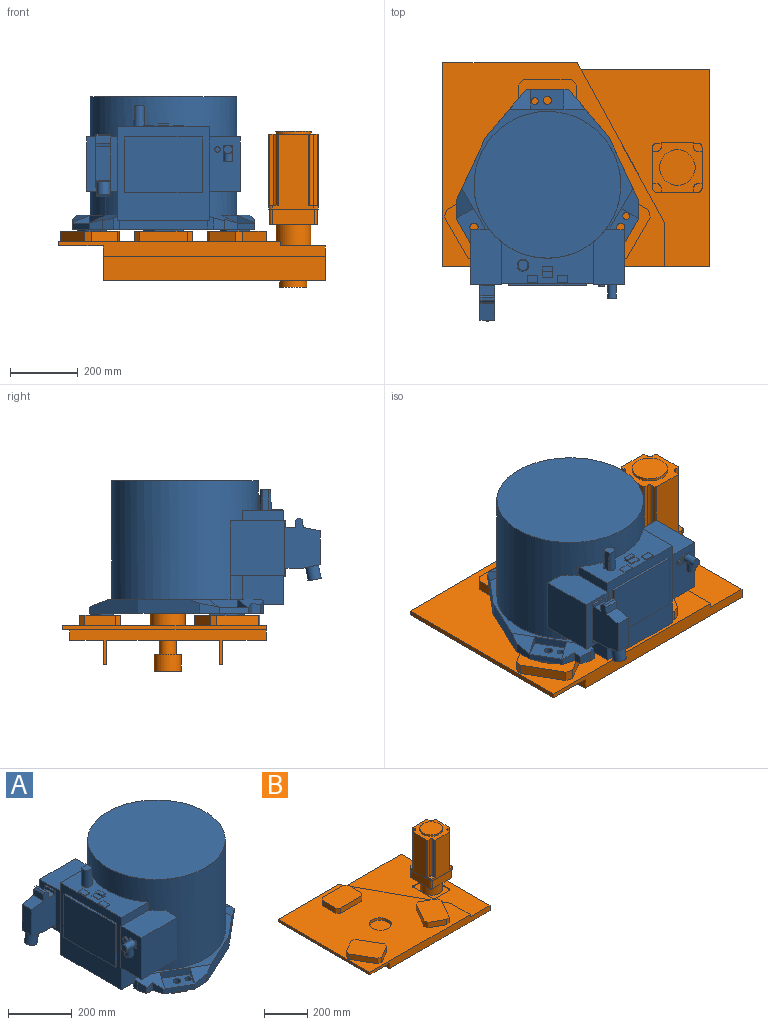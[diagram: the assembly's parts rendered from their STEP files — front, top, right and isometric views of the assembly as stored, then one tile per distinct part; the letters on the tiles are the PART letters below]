
ASSEMBLY  parts=2 mates=2
PART A: 149 faces, bbox 684.3x536x396.9 mm
  f0: plane 133x130.4mm, normal (-0.18,-0.32,0.93), area 3298.5mm2, adj f5,f6,f7,f22,f23,f24,f25,f26
  f1: plane 88.23x49.94mm, normal (-0.18,0.32,0.93), area 2586.9mm2, adj f5,f8,f16,f57
  f2: plane 63.01x59mm, normal (0.37,0,0.93), area 2427.4mm2, adj f5,f9,f20,f51
  f3: plane 536x513.5mm, normal (0,0,-1), area 138421.2mm2, adj f4,f6,f7,f8,f9,f10,f11,f12
  f4: plane 37.86x17.6mm, normal (-1,0,0), area 576mm2, adj f3,f10,f15,f49,f89,f90
  f5: plane 504.71x436.61mm, normal (0,0,1), area 18029.8mm2, adj f0,f1,f2,f13,f16,f20,f21,f48
  f6: plane 57.34x29.39mm, normal (0,-1,0), area 1359.2mm2, adj f0,f3,f21,f22,f50,f63,f64,f65
  f7: plane 37.86x17.6mm, normal (-1,0,0), area 576mm2, adj f0,f3,f12,f23,f76,f90
  f8: plane 57.34x29.39mm, normal (0,1,0), area 1359.2mm2, adj f1,f3,f14,f16,f49,f57,f58,f60
  f9: plane 125x18.04mm, normal (1,0,0), area 2251.1mm2, adj f2,f3,f13,f20,f48,f51,f52,f53
  f10: plane 195x41.4mm, normal (0,-1,0), area 5230.6mm2, adj f3,f4,f11,f71,f75,f90
  f11: plane 259x41.4mm, normal (-1,0,0), area 10722.6mm2, adj f3,f10,f12,f71
  f12: plane 195x41.4mm, normal (0,1,0), area 5230.6mm2, adj f3,f7,f11,f71,f75,f90
  f13: plane 143.59x120.48mm, normal (0.64,0.77,0), area 6860.4mm2, adj f3,f5,f9,f16,f48
  f14: plane 85.81x49.54mm, normal (-0.5,0.87,0), area 1787.5mm2, adj f3,f8,f19,f49
  f15: plane 33.71x32.4mm, normal (-0.97,0.26,0), area 973.2mm2, adj f3,f4,f18,f49
  f16: plane 182.32x85.02mm, normal (0.42,0.91,0), area 8106mm2, adj f1,f3,f5,f8,f13
  f17: plane 29.33x0mm, normal (-1,0,0), area 0mm2, adj f3,f18,f19,f49
  f18: plane 29.33x25.32mm, normal (0,1,0), area 679.3mm2, adj f3,f15,f17,f49
  f19: plane 38.96x29.33mm, normal (-0.97,0.26,0), area 955.3mm2, adj f3,f14,f17,f49
  f20: plane 143.59x120.48mm, normal (0.64,-0.77,0), area 6860.4mm2, adj f2,f3,f5,f9,f21
  f21: plane 182.32x85.02mm, normal (0.42,-0.91,0), area 8106mm2, adj f3,f5,f6,f20,f50
  f22: plane 85.97x49.63mm, normal (-0.5,-0.87,0), area 1790.8mm2, adj f0,f3,f6,f26
  f23: plane 33.71x32.9mm, normal (-0.97,-0.26,0), area 985.8mm2, adj f0,f3,f7,f24
  f24: plane 29.16x25.19mm, normal (0,-1,0), area 671.6mm2, adj f0,f3,f23,f25
  f25: plane 29.16x0mm, normal (-1,0,0), area 0mm2, adj f0,f3,f24,f26
  f26: plane 38.37x29.16mm, normal (-0.97,-0.26,0), area 937.4mm2, adj f0,f3,f22,f25
  f27: plane 46.11x26.62mm, normal (0.5,-0.87,0), area 319.5mm2, adj f3,f28,f32,f33
  f28: cylinder r=630.54mm len=48.29mm, axis (0,0,-1), area 294.9mm2, adj f3,f27,f29,f33
  f29: cylinder r=630.54mm len=47.02mm, axis (0,0,-1), area 287.2mm2, adj f3,f28,f30,f33
  f30: plane 38.79x22.39mm, normal (-0.5,0.87,0), area 268.7mm2, adj f3,f29,f31,f33
  f31: cylinder r=630.54mm len=45.18mm, axis (0,0,-1), area 287.2mm2, adj f3,f30,f32,f33
  f32: cylinder r=630.54mm len=46.38mm, axis (0,0,-1), area 294.9mm2, adj f3,f27,f31,f33
  f33: plane 101.59x83.83mm, normal (0,0,-1), area 4940.6mm2, adj f27,f28,f29,f30,f31,f32,f67,f69
  f34: plane 53.24x6mm, normal (-1,0,0), area 319.5mm2, adj f3,f35,f39,f40
  f35: cylinder r=630.54mm len=37.27mm, axis (0,0,-1), area 294.9mm2, adj f3,f34,f36,f40
  f36: cylinder r=630.54mm len=36.26mm, axis (0,0,-1), area 287.2mm2, adj f3,f35,f37,f40
  f37: plane 44.79x6mm, normal (1,0,0), area 268.7mm2, adj f3,f36,f38,f40
  f38: cylinder r=630.54mm len=36.26mm, axis (0,0,-1), area 287.2mm2, adj f3,f37,f39,f40
  f39: cylinder r=630.54mm len=37.27mm, axis (0,0,-1), area 294.9mm2, adj f3,f34,f38,f40
  f40: plane 117.31x68.5mm, normal (0,0,-1), area 4940.6mm2, adj f34,f35,f36,f37,f38,f39,f55,f56
  f41: plane 46.11x26.62mm, normal (0.5,0.87,0), area 319.5mm2, adj f3,f42,f46,f47
  f42: cylinder r=630.54mm len=46.38mm, axis (0,0,-1), area 294.9mm2, adj f3,f41,f43,f47
  f43: cylinder r=630.54mm len=45.18mm, axis (0,0,-1), area 287.2mm2, adj f3,f42,f44,f47
  f44: plane 38.79x22.39mm, normal (-0.5,-0.87,0), area 268.7mm2, adj f3,f43,f45,f47
  f45: cylinder r=630.54mm len=47.02mm, axis (0,0,-1), area 287.2mm2, adj f3,f44,f46,f47
  f46: cylinder r=630.54mm len=48.29mm, axis (0,0,-1), area 294.9mm2, adj f3,f41,f45,f47
  f47: plane 101.59x83.83mm, normal (0,0,-1), area 4940.6mm2, adj f41,f42,f43,f44,f45,f46,f68,f70
  f48: plane 63.01x59mm, normal (0.37,0,0.93), area 2427.4mm2, adj f5,f9,f13,f52
  f49: plane 133x130.4mm, normal (-0.18,0.32,0.93), area 3279.3mm2, adj f4,f5,f8,f14,f15,f17,f18,f19
  f50: plane 88.23x49.94mm, normal (-0.18,-0.32,0.93), area 2586.9mm2, adj f5,f6,f21,f64
  f51: plane 59x23.4mm, normal (0,1,0), area 691.5mm2, adj f2,f9,f53,f54
  f52: plane 59x23.4mm, normal (0,-1,0), area 691.5mm2, adj f9,f48,f53,f54
  f53: plane 98x59mm, normal (0,0,1), area 5015.5mm2, adj f9,f51,f52,f54,f55,f56
  f54: plane 98x23.4mm, normal (1,0,0), area 2293.2mm2, adj f5,f51,f52,f53
  f55: cylinder r=10mm len=24mm, axis (0,0,-1), area 1508mm2, adj f40,f53
  f56: cylinder r=12mm len=24mm, axis (0,0,-1), area 1809.6mm2, adj f40,f53
  f57: plane 50x28.87mm, normal (-0.87,-0.5,0), area 692.8mm2, adj f1,f5,f8,f60,f61
  f58: plane 82.98x47.91mm, normal (0.5,-0.87,0), area 6.6mm2, adj f8,f49,f59,f60
  f59: plane 51.1x29.5mm, normal (0.87,0.5,0), area 693.2mm2, adj f5,f49,f58,f60,f61
  f60: plane 114.37x99mm, normal (0,0,1), area 5014.1mm2, adj f8,f57,f58,f59,f61,f67,f69
  f61: plane 84.87x49mm, normal (-0.5,0.87,0), area 2293.2mm2, adj f5,f57,f59,f60
  f62: plane 51.1x29.5mm, normal (0.87,-0.5,0), area 693.2mm2, adj f0,f5,f63,f65,f66
  f63: plane 82.98x47.91mm, normal (0.5,0.87,0), area 6.6mm2, adj f0,f6,f62,f65
  f64: plane 50x28.87mm, normal (-0.87,0.5,0), area 692.8mm2, adj f5,f6,f50,f65,f66
  f65: plane 114.37x99mm, normal (0,0,1), area 5014.1mm2, adj f6,f62,f63,f64,f66,f68,f70
  f66: plane 84.87x49mm, normal (-0.5,-0.87,0), area 2293.2mm2, adj f5,f62,f64,f65
  f67: cylinder r=12mm len=24mm, axis (0,0,-1), area 1809.6mm2, adj f33,f60
  f68: cylinder r=12mm len=24mm, axis (0,0,-1), area 1809.6mm2, adj f47,f65
  f69: cylinder r=10mm len=24mm, axis (0,0,-1), area 1508mm2, adj f33,f60
  f70: cylinder r=10mm len=24mm, axis (0,0,-1), area 1508mm2, adj f47,f65
  f71: plane 259x10.43mm, normal (0,0,-1), area 2701.7mm2, adj f10,f11,f12,f75
  f72: cylinder r=216.5mm len=70.62mm, axis (0,0,1), area 3618.9mm2, adj f5,f73,f89,f96
  f73: cylinder r=216.5mm len=433mm, axis (0,0,1), area 379179.2mm2, adj f5,f72,f74,f76,f77,f81,f87,f92
  f74: plane 433x433mm, normal (0,0,1), area 147253.5mm2, adj f73
  f75: plane 259x15.4mm, normal (1,0,0), area 3988.6mm2, adj f10,f12,f71,f90
  f76: plane 121.25x86.02mm, normal (0,-1,0), area 9509.8mm2, adj f0,f5,f7,f73,f88,f90,f119
  f77: plane 121.25x30.98mm, normal (0,1,0), area 3755.6mm2, adj f73,f87,f88,f92
  f78: plane 62.5x19.48mm, normal (0,1,0.05), area 1170.8mm2, adj f79,f80,f87
  f79: cone r=17.5mm half-angle=2deg, axis (0,0,-1), area 5201.3mm2, adj f78,f80,f87
  f80: plane 30.64x27.14mm, normal (0,0,1), area 690.6mm2, adj f78,f79
  f81: plane 121.25x30.98mm, normal (0,-1,0), area 3755.6mm2, adj f73,f87,f88,f116
  f82: plane 230x165mm, normal (-1,0,0), area 37950mm2, adj f83,f84,f85,f86
  f83: plane 230x7.4mm, normal (0,0,-1), area 1702mm2, adj f82,f84,f86,f88
  f84: plane 165x7.4mm, normal (0,1,0), area 1221mm2, adj f82,f83,f85,f88
  f85: plane 230x7.4mm, normal (0,0,1), area 1702mm2, adj f82,f84,f86,f88
  f86: plane 165x7.4mm, normal (0,-1,0), area 1221mm2, adj f82,f83,f85,f88
  f87: plane 270x121.25mm, normal (0,0,1), area 20903.9mm2, adj f73,f77,f78,f79,f81,f88,f133,f134
  f88: plane 277x270mm, normal (-1,0,0), area 36839.8mm2, adj f76,f77,f81,f83,f84,f85,f86,f87
  f89: plane 121.25x86.02mm, normal (0,1,0), area 9509.8mm2, adj f4,f5,f49,f72,f88,f90,f96
  f90: plane 270x244mm, normal (0,0,-1), area 63849.7mm2, adj f4,f7,f10,f12,f75,f76,f88,f89
  f91: plane 44x10mm, normal (-1,0,0), area 440mm2, adj f99,f100,f101,f103
  f92: plane 160x91.56mm, normal (0,0,1), area 13944.5mm2, adj f73,f77,f88,f93,f94,f95,f97
  f93: plane 160x2.38mm, normal (0,-1,0), area 381.1mm2, adj f88,f92,f94,f96
  f94: plane 160x91.56mm, normal (-1,0,0), area 8489.6mm2, adj f92,f93,f95,f96,f98,f99,f100,f101
  f95: plane 160x160mm, normal (0,1,0), area 25600mm2, adj f92,f94,f96,f97
  f96: plane 160x91.56mm, normal (0,0,-1), area 13944.5mm2, adj f72,f88,f89,f93,f94,f95,f97
  f97: plane 160x55.64mm, normal (1,0,0), area 8901.8mm2, adj f73,f92,f95,f96
  f98: plane 44x5mm, normal (0,0,-1), area 220mm2, adj f94,f99,f101,f102
  f99: plane 157.5x106mm, normal (0,1,0), area 12860.7mm2, adj f91,f94,f98,f100,f102,f103,f104,f105
  f100: plane 44x5mm, normal (0,0,1), area 220mm2, adj f91,f94,f99,f101
  f101: plane 157.5x106mm, normal (0,-1,0), area 12860.7mm2, adj f91,f94,f98,f100,f102,f103,f104,f105
  f102: plane 44x10mm, normal (-1,0,0), area 440mm2, adj f98,f99,f101,f105
  f103: plane 44x29mm, normal (0,0,1), area 1276mm2, adj f91,f99,f101,f110
  f104: plane 100.02x44mm, normal (-1,0,0), area 4400.8mm2, adj f99,f101,f106,f107
  f105: plane 51x44mm, normal (0,0,-1), area 2244mm2, adj f99,f101,f102,f106
  f106: plane 50x44mm, normal (-0.2,0,-0.98), area 986.9mm2, adj f99,f101,f104,f105,f109
  f107: plane 50x44mm, normal (-0.2,0,0.98), area 2243.5mm2, adj f99,f101,f104,f112
  f108: plane 40x39.22mm, normal (-0.2,0,-0.98), area 1256.6mm2, adj f109
  f109: cylinder r=20mm len=47.06mm, axis (-0.2,0,-0.98), area 5026.5mm2, adj f106,f108
  f110: plane 44x21.5mm, normal (1,0,0), area 946mm2, adj f99,f101,f103,f113
  f111: plane 44x8.59mm, normal (0,0,1), area 378.1mm2, adj f99,f101,f113,f114
  f112: plane 44x22.02mm, normal (-1,0,0.09), area 972.6mm2, adj f99,f101,f107,f114
  f113: plane 44x6mm, normal (0.71,0,0.71), area 373.4mm2, adj f99,f101,f110,f111
  f114: plane 44x5.48mm, normal (-0.71,0,0.71), area 341mm2, adj f99,f101,f111,f112
  f115: plane 160x2.38mm, normal (0,1,0), area 381.1mm2, adj f88,f116,f118,f119
  f116: plane 160x91.56mm, normal (0,0,1), area 13944.6mm2, adj f73,f81,f115,f117,f118,f120
  f117: plane 160x160mm, normal (0,-1,0), area 25600mm2, adj f116,f118,f119,f120
  f118: plane 160x91.56mm, normal (-1,0,0), area 13746.3mm2, adj f115,f116,f117,f119,f122,f124,f125,f126
  f119: plane 160x91.56mm, normal (0,0,-1), area 13944.6mm2, adj f73,f76,f115,f117,f118,f120
  f120: plane 160x55.64mm, normal (1,0,0), area 8901.9mm2, adj f73,f116,f117,f119
  f121: plane 16x16mm, normal (-1,0,0), area 201.1mm2, adj f122
  f122: cylinder r=8mm len=16mm, axis (-1,0,0), area 377mm2, adj f118,f121
  f123: cylinder r=13mm len=36.25mm, axis (0,0,-1), area 2285mm2, adj f130,f131
  f124: plane 26.5x2.5mm, normal (0,0,-1), area 66.3mm2, adj f118,f125,f127,f128
  f125: plane 26.5x2.5mm, normal (0,1,0), area 66.3mm2, adj f118,f124,f126,f128
  f126: plane 26.5x2.5mm, normal (0,0,1), area 66.3mm2, adj f118,f125,f127,f128
  f127: plane 26.5x2.5mm, normal (0,-1,0), area 66.3mm2, adj f118,f124,f126,f128
  f128: plane 26.5x26.5mm, normal (-1,0,0), area 171.3mm2, adj f124,f125,f126,f127,f130
  f129: plane 26x26mm, normal (-1,0,0), area 530.9mm2, adj f130
  f130: cylinder r=13mm len=39.51mm, axis (-1,0,0), area 2551.2mm2, adj f123,f128,f129
  f131: plane 26x26mm, normal (0,0,-1), area 530.9mm2, adj f123
  f132: plane 30x21.5mm, normal (0,0,1), area 645mm2, adj f133,f134,f135,f136
  f133: plane 30x2.7mm, normal (1,0,0), area 81mm2, adj f87,f132,f134,f136
  f134: plane 21.5x2.7mm, normal (0,1,0), area 58mm2, adj f87,f132,f133,f135
  f135: plane 30x2.7mm, normal (-1,0,0), area 81mm2, adj f87,f132,f134,f136
  f136: plane 21.5x2.7mm, normal (0,-1,0), area 58mm2, adj f87,f132,f133,f135
  f137: plane 30x21.5mm, normal (0,0,1), area 645mm2, adj f138,f139,f140,f141
  f138: plane 30x2.7mm, normal (1,0,0), area 81mm2, adj f87,f137,f139,f141
  f139: plane 21.5x2.7mm, normal (0,1,0), area 58mm2, adj f87,f137,f138,f140
  f140: plane 30x2.7mm, normal (-1,0,0), area 81mm2, adj f87,f137,f139,f141
  f141: plane 21.5x2.7mm, normal (0,-1,0), area 58mm2, adj f87,f137,f138,f140
  f142: plane 30x12.87mm, normal (0,0,1), area 386.1mm2, adj f143,f144,f145,f146
  f143: plane 30x8mm, normal (0,-1,0), area 149.2mm2, adj f87,f142,f145,f146,f147,f148
  f144: plane 30x8mm, normal (0,1,0), area 149.2mm2, adj f87,f142,f145,f146,f147,f148
  f145: plane 30x8mm, normal (1,0,0), area 240mm2, adj f87,f142,f143,f144
  f146: plane 30x5.3mm, normal (-1,0,0), area 159mm2, adj f142,f143,f144,f147
  f147: plane 30x17.13mm, normal (0,0,1), area 513.9mm2, adj f143,f144,f146,f148
  f148: plane 30x2.7mm, normal (-1,0,0), area 81mm2, adj f87,f143,f144,f147
PART B: 108 faces, bbox 785.1x600x460 mm
  f0: plane 655x332mm, normal (0,0,-1), area 215496.5mm2, adj f6,f8,f99,f101,f104
  f1: plane 655x100mm, normal (0,0,-1), area 65500mm2, adj f6,f8,f11,f98
  f2: plane 655.11x600mm, normal (0,0,1), area 264118.6mm2, adj f10,f12,f13,f14,f15,f69,f71,f72
  f3: plane 27.74x27.59mm, normal (0,0,1), area 559mm2, adj f40,f41,f42,f58,f59,f60,f61,f62
  f4: plane 27.75x27.74mm, normal (0,0,1), area 561mm2, adj f38,f39,f40,f53,f54,f55,f56,f57
  f5: plane 27.74x27.69mm, normal (0,0,1), area 560.4mm2, adj f37,f38,f44,f48,f49,f50,f51,f52
  f6: plane 580x101.7mm, normal (-1,0,0), area 18834mm2, adj f0,f1,f7,f10,f11,f16,f98,f99
  f7: plane 655x128mm, normal (0,0,-1), area 83840mm2, adj f6,f8,f10,f102
  f8: plane 580x101.7mm, normal (1,0,0), area 18834mm2, adj f0,f1,f7,f9,f10,f11,f98,f99
  f9: plane 580x378mm, normal (0,0,1), area 116182.9mm2, adj f8,f10,f11,f13,f14,f17,f18,f19
  f10: plane 785.11x43.5mm, normal (0,-1,0), area 28493.9mm2, adj f2,f6,f7,f8,f9,f12,f13,f16
  f11: plane 655x30mm, normal (0,1,0), area 19650mm2, adj f1,f6,f8,f9,f16
  f12: plane 600x13.5mm, normal (-1,0,0), area 8100mm2, adj f2,f10,f15,f16
  f13: plane 127x13.5mm, normal (1,0,0), area 1714.5mm2, adj f2,f9,f10,f14
  f14: plane 473x258.95mm, normal (0.88,0.48,0), area 7279.8mm2, adj f2,f9,f13,f15,f16
  f15: plane 396.16x13.5mm, normal (0,1,0), area 5348.1mm2, adj f2,f12,f14,f16
  f16: plane 600x407.11mm, normal (0,0,-1), area 83494.6mm2, adj f6,f10,f11,f12,f14,f15
  f17: cylinder r=8mm len=8mm, axis (0,0,1), area 62.8mm2, adj f9,f18,f24,f25
  f18: plane 92x5mm, normal (0,1,0), area 460mm2, adj f9,f17,f19,f25
  f19: cylinder r=8mm len=8mm, axis (0,0,1), area 62.8mm2, adj f9,f18,f20,f25
  f20: plane 127x5mm, normal (-1,0,0), area 635mm2, adj f9,f19,f21,f25
  f21: cylinder r=8mm len=8mm, axis (0,0,1), area 62.8mm2, adj f9,f20,f22,f25
  f22: plane 92x5mm, normal (0,-1,0), area 460mm2, adj f9,f21,f23,f25
  f23: cylinder r=8mm len=8mm, axis (0,0,1), area 62.8mm2, adj f9,f22,f24,f25
  f24: plane 127x5mm, normal (1,0,0), area 635mm2, adj f9,f17,f23,f25
  f25: plane 143x108mm, normal (0,0,1), area 7056.8mm2, adj f17,f18,f19,f20,f21,f22,f23,f24
  f26: cylinder r=51.5mm len=103mm, axis (0,0,-1), area 21680.1mm2, adj f25,f35
  f27: cylinder r=8mm len=47mm, axis (0,0,-1), area 590.6mm2, adj f28,f34,f35,f36
  f28: plane 124x47mm, normal (0,-1,0), area 5828mm2, adj f27,f29,f35,f36
  f29: cylinder r=8mm len=47mm, axis (0,0,-1), area 590.6mm2, adj f28,f30,f35,f36
  f30: plane 124x47mm, normal (1,0,0), area 5828mm2, adj f29,f31,f35,f36
  f31: cylinder r=8mm len=47mm, axis (0,0,-1), area 590.6mm2, adj f30,f32,f35,f36
  f32: plane 124x47mm, normal (0,1,0), area 5828mm2, adj f31,f33,f35,f36
  f33: cylinder r=8mm len=47mm, axis (0,0,-1), area 590.6mm2, adj f32,f34,f35,f36
  f34: plane 124x47mm, normal (-1,0,0), area 5828mm2, adj f27,f33,f35,f36
  f35: plane 140x140mm, normal (0,0,-1), area 11212.8mm2, adj f26,f27,f28,f29,f30,f31,f32,f33
  f36: plane 145.6x145.6mm, normal (0,0,-1), area 1520.2mm2, adj f27,f28,f29,f30,f31,f32,f33,f34
  f37: cylinder r=12.5mm len=12.5mm, axis (0,0,-1), area 216mm2, adj f5,f36,f38,f44
  f38: plane 221x120.6mm, normal (0,-1,0), area 20261.8mm2, adj f4,f5,f36,f37,f39,f52,f53,f66
  f39: cylinder r=12.5mm len=12.5mm, axis (0,0,-1), area 216mm2, adj f4,f36,f38,f40
  f40: plane 221x120.6mm, normal (1,0,0), area 20252.2mm2, adj f3,f4,f36,f39,f41,f57,f58,f66
  f41: cylinder r=12.5mm len=12.5mm, axis (0,0,-1), area 216mm2, adj f3,f36,f40,f42
  f42: plane 221x120.6mm, normal (0,1,0), area 20285.8mm2, adj f3,f36,f41,f43,f45,f62,f63,f66
  f43: cylinder r=12.5mm len=12.5mm, axis (0,0,-1), area 216mm2, adj f36,f42,f44,f45
  f44: plane 221x120.6mm, normal (-1,0,0), area 20251.1mm2, adj f5,f36,f37,f43,f45,f47,f48,f66
  f45: plane 27.74x27.73mm, normal (0,0,1), area 561mm2, adj f42,f43,f44,f46,f47,f63,f64,f65
  f46: plane 210x10.04mm, normal (0,1,0), area 2107.5mm2, adj f45,f47,f65,f66
  f47: cylinder r=2.74mm len=210mm, axis (0,0,-1), area 905.5mm2, adj f44,f45,f46,f66
  f48: cylinder r=2.74mm len=210mm, axis (0,0,-1), area 905.5mm2, adj f5,f44,f49,f66
  f49: plane 210x10.06mm, normal (0,-1,0), area 2111.7mm2, adj f5,f48,f50,f66
  f50: cylinder r=12.5mm len=210mm, axis (0,0,-1), area 3808.2mm2, adj f5,f49,f51,f66
  f51: plane 210x10.95mm, normal (-1,0,0), area 2300.2mm2, adj f5,f50,f52,f66
  f52: cylinder r=2.74mm len=210mm, axis (0,0,-1), area 905.5mm2, adj f5,f38,f51,f66
  f53: cylinder r=2.74mm len=210mm, axis (0,0,-1), area 905.5mm2, adj f4,f38,f54,f66
  f54: plane 210x9.76mm, normal (1,0,0), area 2048.6mm2, adj f4,f53,f55,f66
  f55: cylinder r=12.5mm len=210mm, axis (0,0,-1), area 4017.8mm2, adj f4,f54,f56,f66
  f56: plane 210x10.26mm, normal (0,-1,0), area 2154.1mm2, adj f4,f55,f57,f66
  f57: cylinder r=2.74mm len=210mm, axis (0,0,-1), area 905.5mm2, adj f4,f40,f56,f66
  f58: cylinder r=2.74mm len=210mm, axis (0,0,-1), area 905.5mm2, adj f3,f40,f59,f66
  f59: plane 210x9.56mm, normal (0,1,0), area 2006.7mm2, adj f3,f58,f60,f66
  f60: cylinder r=12.5mm len=210mm, axis (0,0,-1), area 3748.4mm2, adj f3,f59,f61,f66
  f61: plane 210x11.73mm, normal (1,0,0), area 2463.6mm2, adj f3,f60,f62,f66
  f62: cylinder r=2.74mm len=210mm, axis (0,0,-1), area 905.5mm2, adj f3,f42,f61,f66
  f63: cylinder r=2.74mm len=210mm, axis (0,0,-1), area 906.4mm2, adj f42,f45,f64,f66
  f64: plane 210x9.73mm, normal (-1,0,0), area 2043.7mm2, adj f45,f63,f65,f66
  f65: cylinder r=12.5mm len=210mm, axis (0,0,-1), area 4068.4mm2, adj f45,f46,f64,f66
  f66: plane 145.6x145.6mm, normal (0,0,1), area 10164.8mm2, adj f38,f40,f42,f44,f46,f47,f48,f49
  f67: cylinder r=52.5mm len=105mm, axis (0,0,-1), area 2638.9mm2, adj f66,f68
  f68: plane 105x105mm, normal (0,0,1), area 8659mm2, adj f67
  f69: cylinder r=50mm len=100mm, axis (0,0,1), area 4241.2mm2, adj f2,f70
  f70: plane 100x100mm, normal (0,0,1), area 7854mm2, adj f69
  f71: plane 90x30mm, normal (-1,0,0), area 2700mm2, adj f2,f75,f86,f91
  f72: plane 140x30mm, normal (0,-1,0), area 4200mm2, adj f2,f75,f91,f92
  f73: plane 90x30mm, normal (1,0,0), area 2700mm2, adj f2,f75,f92,f97
  f74: plane 140x30mm, normal (0,1,0), area 4200mm2, adj f2,f75,f86,f97
  f75: plane 170x120mm, normal (0,0,1), area 19950mm2, adj f71,f72,f73,f74,f86,f91,f92,f97
  f76: plane 77.94x45mm, normal (-0.5,0.87,0), area 2700mm2, adj f2,f80,f87,f88
  f77: plane 121.24x70mm, normal (-0.87,-0.5,0), area 4200mm2, adj f2,f80,f88,f89
  f78: plane 77.94x45mm, normal (0.5,-0.87,0), area 2700mm2, adj f2,f80,f89,f90
  f79: plane 121.24x70mm, normal (0.87,0.5,0), area 4200mm2, adj f2,f80,f87,f90
  f80: plane 192.22x173.92mm, normal (0,0,1), area 19950mm2, adj f76,f77,f78,f79,f87,f88,f89,f90
  f81: plane 77.94x45mm, normal (-0.5,-0.87,0), area 2700mm2, adj f2,f85,f94,f95
  f82: plane 121.24x70mm, normal (0.87,-0.5,0), area 4200mm2, adj f2,f85,f93,f94
  f83: plane 77.94x45mm, normal (0.5,0.87,0), area 2700mm2, adj f2,f85,f93,f96
  f84: plane 121.24x70mm, normal (-0.87,0.5,0), area 4200mm2, adj f2,f85,f95,f96
  f85: plane 192.22x173.92mm, normal (0,0,1), area 19950mm2, adj f81,f82,f83,f84,f93,f94,f95,f96
  f86: plane 30x15mm, normal (-0.71,0.71,0), area 636.4mm2, adj f2,f71,f74,f75
  f87: plane 30x20.49mm, normal (0.26,0.97,0), area 636.4mm2, adj f2,f76,f79,f80
  f88: plane 30x20.49mm, normal (-0.97,0.26,0), area 636.4mm2, adj f2,f76,f77,f80
  f89: plane 30x20.49mm, normal (-0.26,-0.97,0), area 636.4mm2, adj f2,f77,f78,f80
  f90: plane 30x20.49mm, normal (0.97,-0.26,0), area 636.4mm2, adj f2,f78,f79,f80
  f91: plane 30x15mm, normal (-0.71,-0.71,0), area 636.4mm2, adj f2,f71,f72,f75
  f92: plane 30x15mm, normal (0.71,-0.71,0), area 636.4mm2, adj f2,f72,f73,f75
  f93: plane 30x20.49mm, normal (0.97,0.26,0), area 636.4mm2, adj f2,f82,f83,f85
  f94: plane 30x20.49mm, normal (0.26,-0.97,0), area 636.4mm2, adj f2,f81,f82,f85
  f95: plane 30x20.49mm, normal (-0.97,-0.26,0), area 636.4mm2, adj f2,f81,f84,f85
  f96: plane 30x20.49mm, normal (-0.26,0.97,0), area 636.4mm2, adj f2,f83,f84,f85
  f97: plane 30x15mm, normal (0.71,0.71,0), area 636.4mm2, adj f2,f73,f74,f75
  f98: plane 655x71.7mm, normal (0,1,0), area 46963.5mm2, adj f1,f6,f8,f100
  f99: plane 655x71.7mm, normal (0,-1,0), area 46963.5mm2, adj f0,f6,f8,f100
  f100: plane 655x10mm, normal (0,0,-1), area 6550mm2, adj f6,f8,f98,f99
  f101: plane 655x71.7mm, normal (0,1,0), area 46963.5mm2, adj f0,f6,f8,f103
  f102: plane 655x71.7mm, normal (0,-1,0), area 46963.5mm2, adj f6,f7,f8,f103
  f103: plane 655x10mm, normal (0,0,-1), area 6550mm2, adj f6,f8,f101,f102
  f104: cylinder r=25mm len=50mm, axis (0,0,1), area 6597.3mm2, adj f0,f107
  f105: cylinder r=40mm len=80mm, axis (0,0,1), area 12566.4mm2, adj f106,f107
  f106: plane 80x80mm, normal (0,0,-1), area 5026.5mm2, adj f105
  f107: plane 80x80mm, normal (0,0,1), area 3063.1mm2, adj f104,f105
PLACE A rot(axis=(0,0,1),90deg) t=(0,0,30)mm
PLACE B t=(113.9,340.5,-43.5)mm
MATE slider A.f72 <-> B.f69  axis (0,0,1) through (0,0,252.16)mm
MATE parallel A.f56 <-> B.f75  axis (0,0,-1) through (0,250,30)mm
